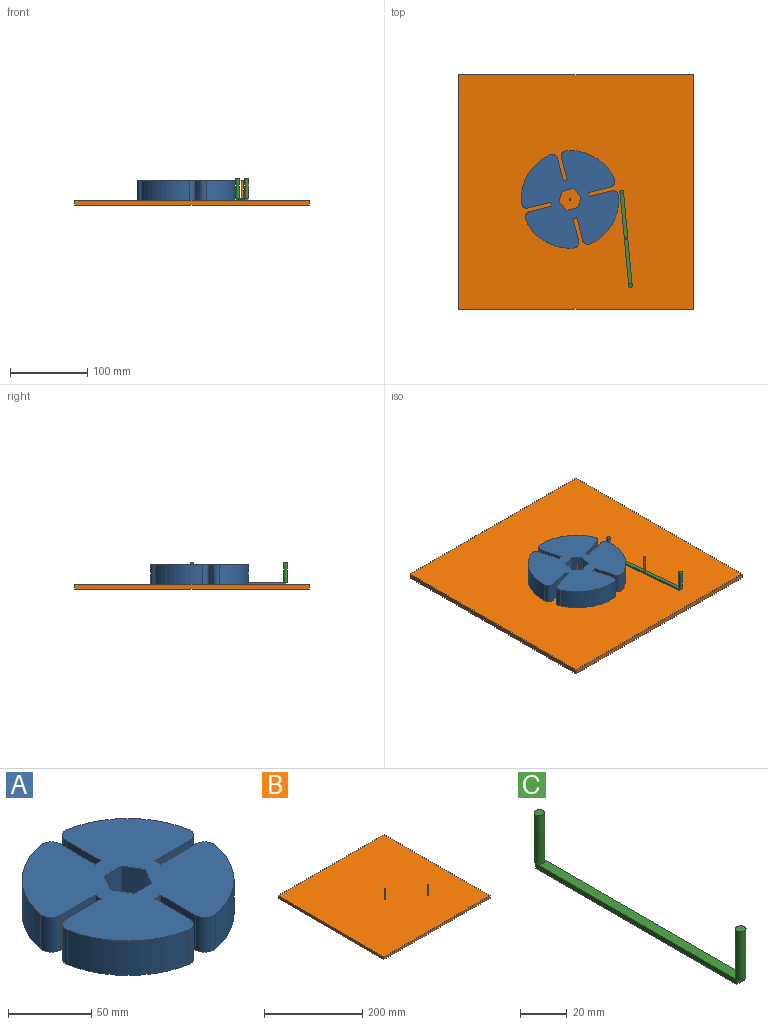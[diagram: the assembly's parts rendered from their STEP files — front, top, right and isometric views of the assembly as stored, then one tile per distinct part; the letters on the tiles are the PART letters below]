
ASSEMBLY  parts=3 mates=2
PART A: 32 faces, bbox 125.1x125.1x25.4 mm
  f0: plane 29.6x25.4mm, normal (1,0,0), area 751.8mm2, adj f15,f16,f17,f24
  f1: cylinder r=63.5mm len=50.9mm, axis (0,0,-1), area 1943.7mm2, adj f16,f17,f24,f25
  f2: plane 29.6x25.4mm, normal (0,-1,0), area 751.8mm2, adj f3,f16,f17,f25
  f3: plane 25.4x5.08mm, normal (-1,0,0), area 129mm2, adj f2,f4,f16,f17
  f4: plane 29.6x25.4mm, normal (0,1,0), area 751.8mm2, adj f3,f16,f17,f26
  f5: cylinder r=63.5mm len=50.9mm, axis (0,0,-1), area 1943.7mm2, adj f16,f17,f26,f27
  f6: plane 29.6x25.4mm, normal (1,0,0), area 751.8mm2, adj f7,f16,f17,f27
  f7: plane 25.4x5.08mm, normal (0,-1,0), area 129mm2, adj f6,f8,f16,f17
  f8: plane 29.6x25.4mm, normal (-1,0,0), area 751.8mm2, adj f7,f16,f17,f28
  f9: cylinder r=63.5mm len=50.9mm, axis (0,0,-1), area 1943.7mm2, adj f16,f17,f28,f29
  f10: plane 29.6x25.4mm, normal (0,1,0), area 751.8mm2, adj f11,f16,f17,f29
  f11: plane 25.4x5.08mm, normal (1,0,0), area 129mm2, adj f10,f12,f16,f17
  f12: plane 29.6x25.4mm, normal (0,-1,0), area 751.8mm2, adj f11,f16,f17,f30
  f13: cylinder r=63.5mm len=50.9mm, axis (0,0,-1), area 1943.7mm2, adj f16,f17,f30,f31
  f14: plane 29.6x25.4mm, normal (-1,0,0), area 751.8mm2, adj f15,f16,f17,f31
  f15: plane 25.4x5.08mm, normal (0,1,0), area 129mm2, adj f0,f14,f16,f17
  f16: plane 125.14x125.14mm, normal (0,0,1), area 11199mm2, adj f0,f1,f2,f3,f4,f5,f6,f7
  f17: plane 125.14x125.14mm, normal (0,0,-1), area 11199mm2, adj f0,f1,f2,f3,f4,f5,f6,f7
  f18: plane 25.4x14.66mm, normal (0,-1,0), area 372.5mm2, adj f16,f17,f19,f23
  f19: plane 25.4x12.7mm, normal (0.87,-0.5,0), area 372.5mm2, adj f16,f17,f18,f20
  f20: plane 25.4x12.7mm, normal (0.87,0.5,0), area 372.5mm2, adj f16,f17,f19,f21
  f21: plane 25.4x14.66mm, normal (0,1,0), area 372.5mm2, adj f16,f17,f20,f22
  f22: plane 25.4x12.7mm, normal (-0.87,0.5,0), area 372.5mm2, adj f16,f17,f21,f23
  f23: plane 25.4x12.7mm, normal (-0.87,-0.5,0), area 372.5mm2, adj f16,f17,f18,f22
  f24: cylinder r=7.62mm len=25.4mm, axis (0,0,-1), area 339.4mm2, adj f0,f1,f16,f17
  f25: cylinder r=7.62mm len=25.4mm, axis (0,0,-1), area 339.4mm2, adj f1,f2,f16,f17
  f26: cylinder r=7.62mm len=25.4mm, axis (0,0,-1), area 339.4mm2, adj f4,f5,f16,f17
  f27: cylinder r=7.62mm len=25.4mm, axis (0,0,-1), area 339.4mm2, adj f5,f6,f16,f17
  f28: cylinder r=7.62mm len=25.4mm, axis (0,0,-1), area 339.4mm2, adj f8,f9,f16,f17
  f29: cylinder r=7.62mm len=25.4mm, axis (0,0,-1), area 339.4mm2, adj f9,f10,f16,f17
  f30: cylinder r=7.62mm len=25.4mm, axis (0,0,-1), area 339.4mm2, adj f12,f13,f16,f17
  f31: cylinder r=7.62mm len=25.4mm, axis (0,0,-1), area 339.4mm2, adj f13,f14,f16,f17
PART B: 10 faces, bbox 304.8x304.8x31.8 mm
  f0: plane 304.8x6.35mm, normal (0,1,0), area 1935.5mm2, adj f1,f3,f4,f5
  f1: plane 304.8x6.35mm, normal (-1,0,0), area 1935.5mm2, adj f0,f2,f4,f5
  f2: plane 304.8x6.35mm, normal (0,-1,0), area 1935.5mm2, adj f1,f3,f4,f5
  f3: plane 304.8x6.35mm, normal (1,0,0), area 1935.5mm2, adj f0,f2,f4,f5
  f4: plane 304.8x304.8mm, normal (0,0,1), area 92891.7mm2, adj f0,f1,f2,f3,f6,f8
  f5: plane 304.8x304.8mm, normal (0,0,-1), area 92903mm2, adj f0,f1,f2,f3
  f6: cylinder r=1.27mm len=25.4mm, axis (0,0,-1), area 202.7mm2, adj f4,f7
  f7: plane 2.54x2.54mm, normal (0,0,1), area 5.1mm2, adj f6
  f8: cylinder r=1.41mm len=25.4mm, axis (0,0,-1), area 224.9mm2, adj f4,f9
  f9: plane 2.82x2.82mm, normal (0,0,1), area 6.2mm2, adj f8
PART C: 12 faces, bbox 4.6x126.5x27.9 mm
  f0: plane 121.92x4.57mm, normal (0,0,1), area 541mm2, adj f2,f4,f6,f10
  f1: plane 4.57x2.54mm, normal (0,1,0), area 11.6mm2, adj f2,f4,f5,f8
  f2: plane 121.92x2.54mm, normal (-1,0,0), area 309.7mm2, adj f0,f1,f3,f5
  f3: plane 4.57x2.54mm, normal (0,-1,0), area 11.6mm2, adj f2,f4,f5,f9
  f4: plane 121.92x2.54mm, normal (1,0,0), area 309.7mm2, adj f0,f1,f3,f5
  f5: plane 121.92x4.57mm, normal (0,0,-1), area 557.4mm2, adj f1,f2,f3,f4
  f6: cylinder r=2.29mm len=25.4mm, axis (0,0,-1), area 364.8mm2, adj f0,f7,f8
  f7: plane 4.57x4.57mm, normal (0,0,1), area 16.4mm2, adj f6
  f8: plane 4.57x2.29mm, normal (0,0,-1), area 8.2mm2, adj f1,f6
  f9: plane 4.57x2.29mm, normal (0,0,-1), area 8.2mm2, adj f3,f10
  f10: cylinder r=2.29mm len=25.4mm, axis (0,0,-1), area 364.8mm2, adj f0,f9,f11
  f11: plane 4.57x4.57mm, normal (0,0,1), area 16.4mm2, adj f10
PLACE A rot(axis=(0,0,1),14.3deg) t=(-32.7,-17.03,0.96)mm
PLACE B t=(-24.92,-7.39,-5.39)mm fixed
PLACE C rot(axis=(0,0,1),5.4deg) t=(40.11,-68.03,0.96)mm
MATE revolute C.f5 <-> B.f8  axis (0,0,-1) through (40.11,-68.03,0.96)mm
MATE revolute A.f9 <-> B.f6  axis (0,0,1) through (-32.7,-17.03,26.36)mm
